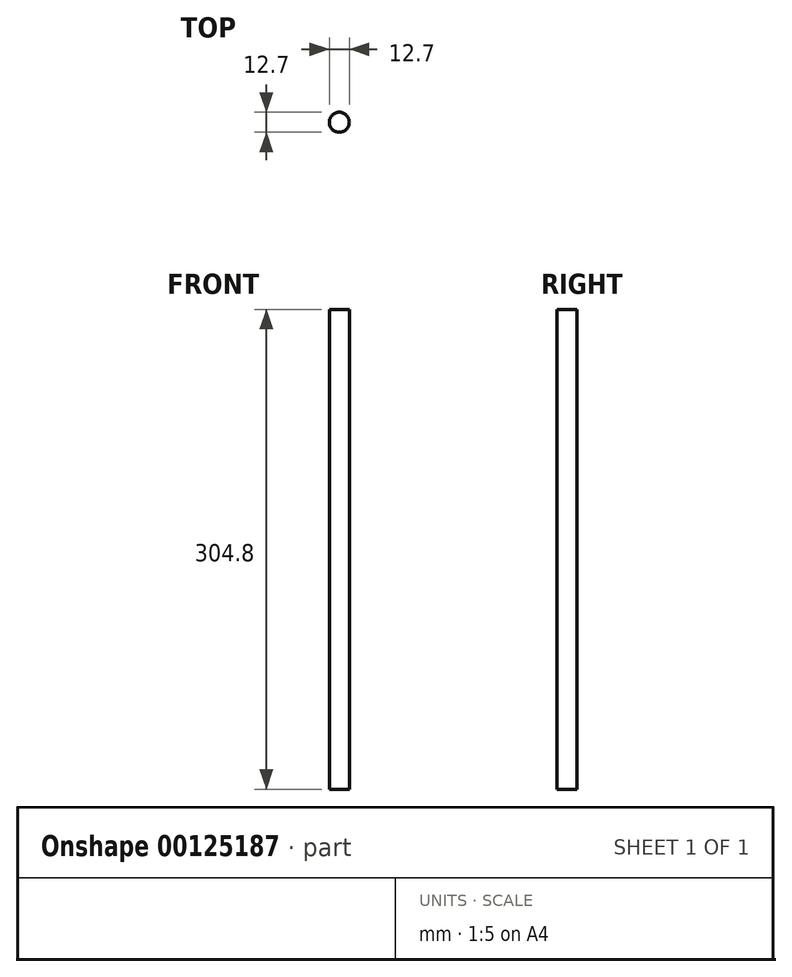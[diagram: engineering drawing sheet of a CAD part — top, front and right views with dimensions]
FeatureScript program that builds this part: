
annotation { "Feature Type Name" : "Feature", "Feature Type Description" : "" }
export const myFeature = defineFeature(function(context is Context, id is Id, definition is map)
    precondition{}
    {
        {
            var Q0;
            Q0=qCreatedBy(makeId("Top.planeOp"),FACE);
            var sketch = newSketch(context, id + "F0", { "sketchPlane" : qUnion([Q0])});
            skCircle(sketch, "E0", {"center": v(0, 0) * mm, "radius": 6.35 * mm});
            skSolve(sketch);
        }
        {
            var Q0;
            Q0 = qSketchRegion(id + "F0", true);
            extrude(context, id + "F1", {"entities" : qUnion([Q0]), "depth" : 304.8 * mm});
        }
    });
